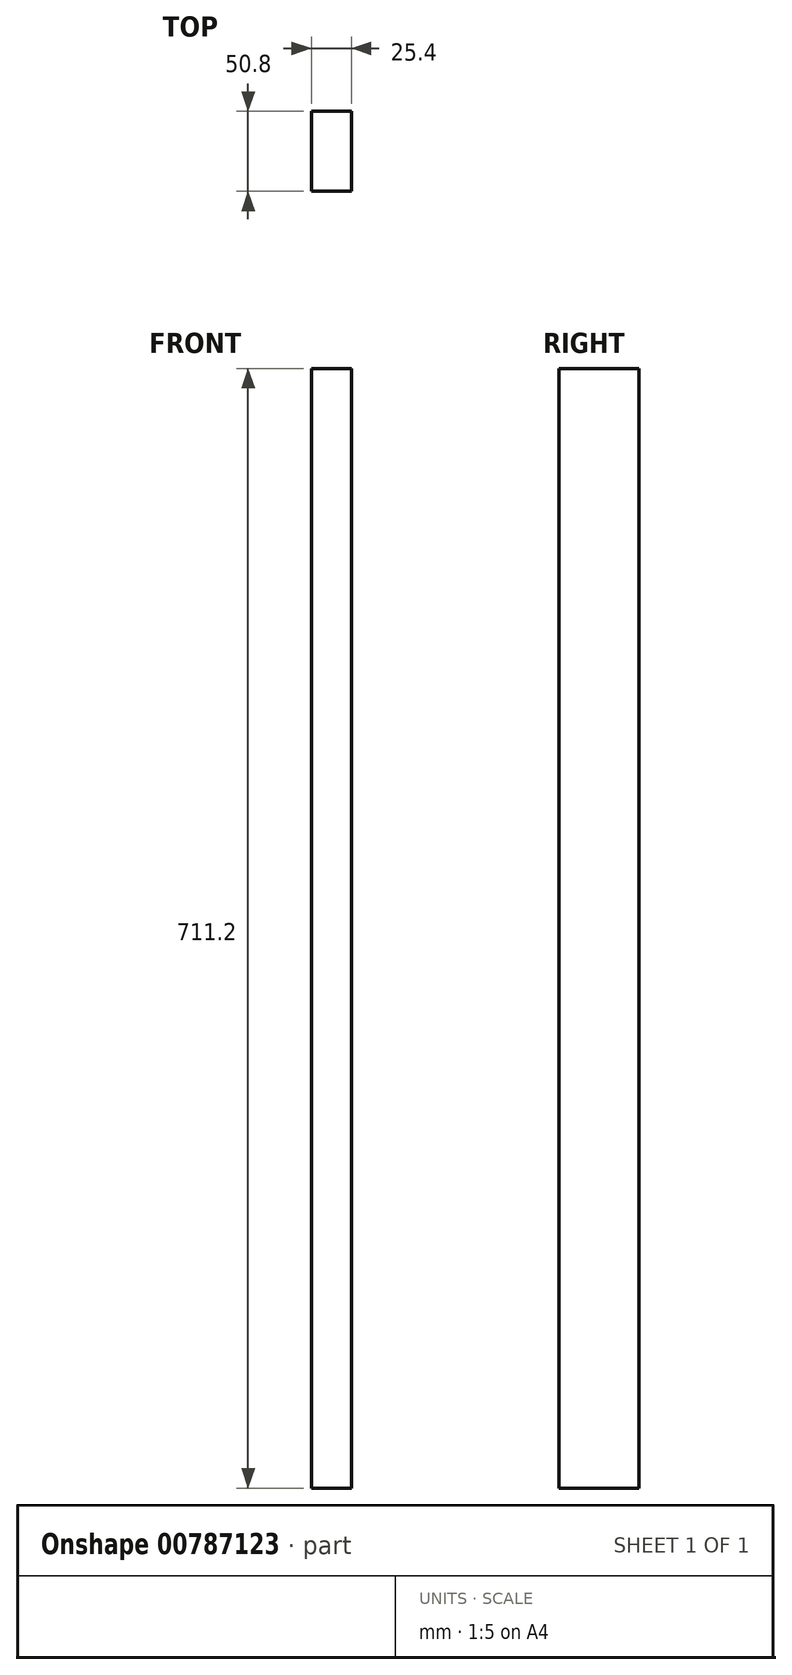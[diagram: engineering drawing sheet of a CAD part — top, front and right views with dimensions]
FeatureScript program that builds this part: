
annotation { "Feature Type Name" : "Feature", "Feature Type Description" : "" }
export const myFeature = defineFeature(function(context is Context, id is Id, definition is map)
    precondition{}
    {
        {
            var Q0;
            Q0=qCreatedBy(makeId("Top.planeOp"),FACE);
            var sketch = newSketch(context, id + "F0", { "sketchPlane" : qUnion([Q0])});
            skLineSegment(sketch, "E0.bottom", {"start": v(12.7, 25.4) * mm, "end": v(-12.7, 25.4) * mm});
            skLineSegment(sketch, "E0.top", {"start": v(12.7, -25.4) * mm, "end": v(-12.7, -25.4) * mm});
            skLineSegment(sketch, "E0.left", {"start": v(12.7, 25.4) * mm, "end": v(12.7, -25.4) * mm});
            skLineSegment(sketch, "E0.right", {"start": v(-12.7, 25.4) * mm, "end": v(-12.7, -25.4) * mm});
            skPoint(sketch, "E0.middle", {"position": v(0, 0) * mm});
            skSolve(sketch);
        }
        {
            var Q0;
            Q0 = qSketchRegion(id + "F0", true);
            extrude(context, id + "F1", {"entities" : qUnion([Q0]), "endBound" : BoundingType.SYMMETRIC, "depth" : 711.2 * mm, "offsetDistance" : 25.4 * mm});
        }
    });
